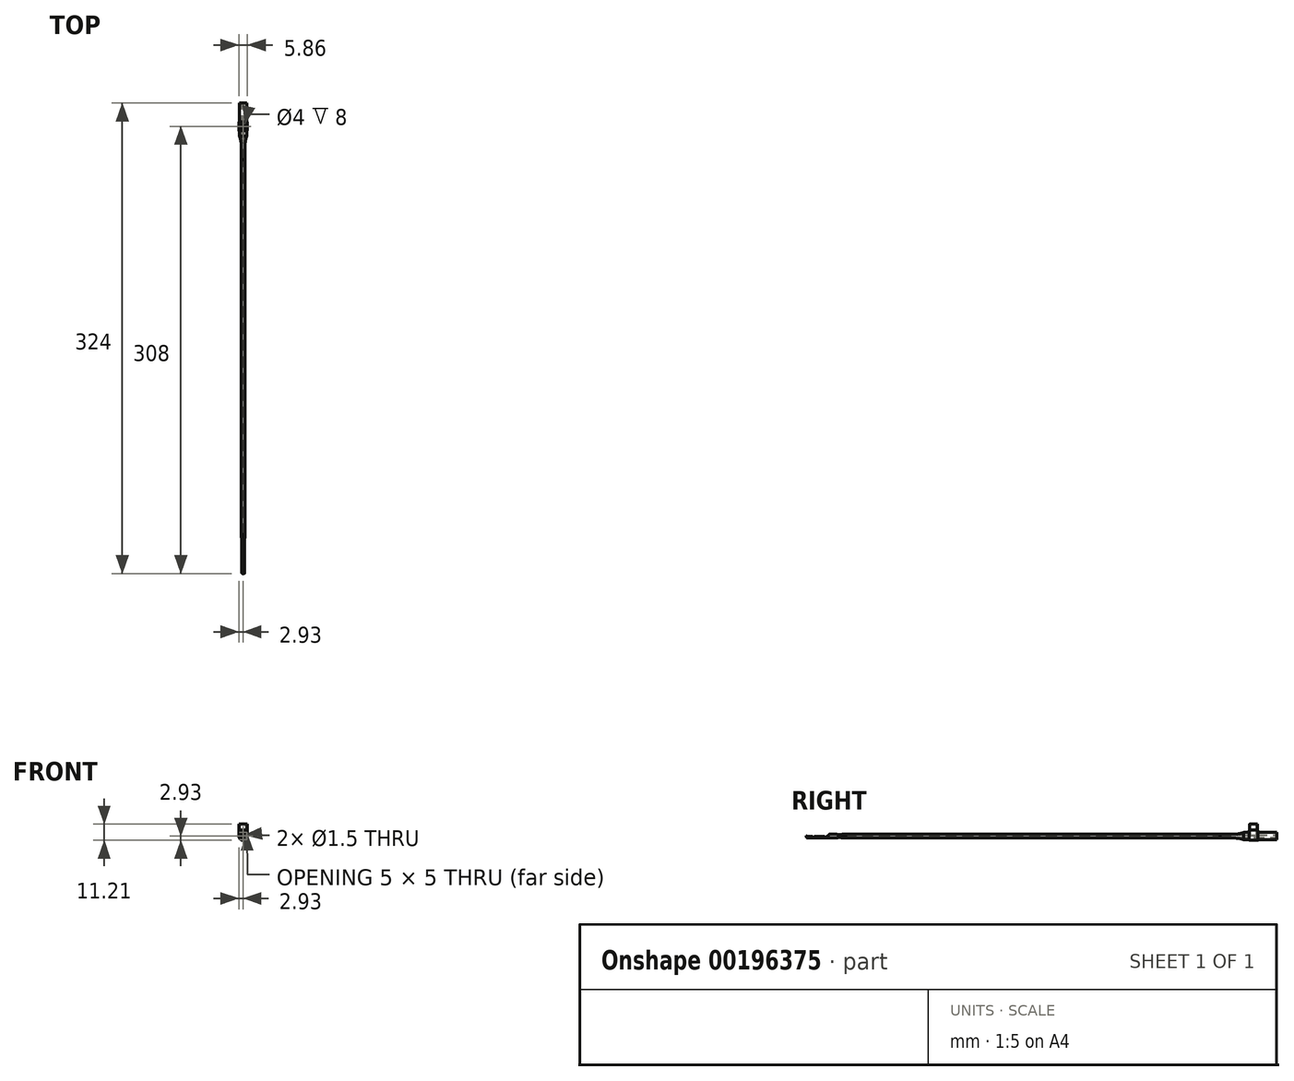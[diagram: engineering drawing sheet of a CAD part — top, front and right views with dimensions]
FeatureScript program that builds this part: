
annotation { "Feature Type Name" : "Feature", "Feature Type Description" : "" }
export const myFeature = defineFeature(function(context is Context, id is Id, definition is map)
    precondition{}
    {
        {
            var Q0;
            Q0=qCreatedBy(makeId("Front.planeOp"),FACE);
            var sketch = newSketch(context, id + "F0", { "sketchPlane" : qUnion([Q0])});
            skCircle(sketch, "E0", {"center": v(0, 0) * mm, "radius": 1.35 * mm});
            skSolve(sketch);
        }
        {
            var Q0;
            Q0=makeQuery(id+"F0.imprint","IMPRINT",FACE,{"disambiguationData":[TD([[makeQuery(id+"F0.imprint","IMPRINT",EDGE,{"derivedFrom":sQuery(id+"F0.wireOp",EDGE,"E0")}),1.0]])]});
            extrude(context, id + "F1", {"entities" : qUnion([Q0]), "depth" : 258 * mm});
        }
        {
            var Q0;
            Q0=qCreatedBy(makeId("Top.planeOp"),FACE);
            var sketch = newSketch(context, id + "F2", { "sketchPlane" : qUnion([Q0])});
            skLineSegment(sketch, "E1.0", {"start": v(1.35, 0) * mm, "end": v(0, 0) * mm});
            skLineSegment(sketch, "E2", {"start": v(1.35, 0) * mm, "end": v(1.35, 10.1) * mm});
            skLineSegment(sketch, "E3", {"start": v(2.5, 20) * mm, "end": v(0, 20) * mm});
            skLineSegment(sketch, "E4", {"start": v(2.52, 16.1) * mm, "end": v(2.5, 20) * mm});
            skArc(sketch, "E5", {"start": v(2.52, 16.1) * mm, "mid": v(1.65, 13.16) * mm, "end": v(1.35, 10.1) * mm});
            skLineSegment(sketch, "E6", {"start": v(0, 0) * mm, "end": v(0, 20) * mm, "construction": true});
            skPoint(sketch, "E7.start.orphan", {"position": v(-1.35, 0) * mm});
            skPoint(sketch, "E8.start.orphan", {"position": v(-1.35, 10.1) * mm});
            skPoint(sketch, "E9.start.orphan", {"position": v(-2.5, 16.1) * mm});
            skPoint(sketch, "E10.orphan", {"position": v(-2.5, 20) * mm});
            skLineSegment(sketch, "E11", {"start": v(0, 0) * mm, "end": v(0, 20) * mm});
            skSolve(sketch);
        }
        {
            var Q0;
            Q0 = qSketchRegion(id + "F2", true);
            var Q1;
            Q1=sQuery(id+"F2.wireOp",EDGE,"E6");
            revolve(context, id + "F3", {"entities" : qUnion([Q0]), "axis" : qUnion([Q1]), "revolveType" : RevolveType.FULL});
        }
        {
            var Q0;
            Q0=makeQuery(id+"F3.opRevolve","SWEPT_FACE",FACE,{"disambiguationData":[OSD([sQuery(id+"F2.wireOp",EDGE,"E3")])]});
            var sketch = newSketch(context, id + "F4", { "sketchPlane" : qUnion([Q0])});
            skArc(sketch, "E12", {"start": v(-2.93, 0) * mm, "mid": v(0, -2.93) * mm, "end": v(2.93, 0) * mm});
            skLineSegment(sketch, "E13", {"start": v(-2.93, 0) * mm, "end": v(-2.93, 4.07) * mm});
            skLineSegment(sketch, "E14", {"start": v(-2.93, 4.07) * mm, "end": v(2.92, 4.07) * mm});
            skLineSegment(sketch, "E15", {"start": v(2.92, 4.07) * mm, "end": v(2.93, 0) * mm});
            skCircle(sketch, "E16.0", {"center": v(0, 0) * mm, "radius": 2.5 * mm});
            skSolve(sketch);
        }
        {
            var Q0;
            Q0 = qSketchRegion(id + "F4", true);
            extrude(context, id + "F5", {"entities" : qUnion([Q0]), "operationType" : NewBodyOperationType.ADD, "depth" : 6 * mm});
        }
        {
            var Q0;
            Q0=makeQuery(id+"F5.opExtrude","SWEPT_FACE",FACE,{"disambiguationData":[OSD([sQuery(id+"F4.wireOp",EDGE,"E14")])]});
            var sketch = newSketch(context, id + "F6", { "sketchPlane" : qUnion([Q0])});
            skCircle(sketch, "E17", {"center": v(0, 23) * mm, "radius": 2.75 * mm});
            skSolve(sketch);
        }
        {
            var Q0;
            Q0 = qSketchRegion(id + "F6", true);
            extrude(context, id + "F7", {"entities" : qUnion([Q0]), "operationType" : NewBodyOperationType.ADD, "depth" : 4.2 * mm});
        }
        {
            var Q0;
            Q0=makeQuery(id+"F5.opExtrude","SWEPT_EDGE",EDGE,{"disambiguationData":[OSD([sQuery(id+"F4.wireOp",EDGE,"E13"),sQuery(id+"F4.wireOp",EDGE,"E14")])]});
            var Q1;
            Q1=makeQuery(id+"F5.opExtrude","SWEPT_EDGE",EDGE,{"disambiguationData":[OSD([sQuery(id+"F4.wireOp",EDGE,"E14"),sQuery(id+"F4.wireOp",EDGE,"E15")])]});
            var Q2;
            Q2=makeQuery(id+"F5.opExtrude","CAP_EDGE",EDGE,{"disambiguationData":[OSD([sQuery(id+"F4.wireOp",EDGE,"E14")])],"isStart":true});
            var Q3;
            Q3=makeQuery(id+"F5.opExtrude","CAP_EDGE",EDGE,{"disambiguationData":[OSD([sQuery(id+"F4.wireOp",EDGE,"E14")])],"isStart":false});
            fillet(context, id + "F8", {"entities" : qUnion([Q0, Q1, Q2, Q3]), "radius" : 1 * mm, "tangentPropagation" : true, "allowEdgeOverflow" : false});
        }
        {
            var Q0;
            Q0=makeQuery(id+"F3.opRevolve","SWEPT_FACE",FACE,{"disambiguationData":[OSD([sQuery(id+"F2.wireOp",EDGE,"E3")])]});
            extrude(context, id + "F9", {"entities" : qUnion([Q0]), "operationType" : NewBodyOperationType.ADD, "depth" : 19 * mm});
        }
        {
            var Q0;
            Q0=makeQuery(id+"F7.opExtrude","CAP_FACE",FACE,{"disambiguationData":[OSD([sQuery(id+"F6.wireOp",EDGE,"E17")])],"isStart":false});
            var sketch = newSketch(context, id + "F10", { "sketchPlane" : qUnion([Q0])});
            skCircle(sketch, "E18", {"center": v(0, 23) * mm, "radius": 2 * mm});
            skSolve(sketch);
        }
        {
            var Q0;
            Q0 = qSketchRegion(id + "F10", true);
            extrude(context, id + "F11", {"entities" : qUnion([Q0]), "operationType" : NewBodyOperationType.REMOVE, "oppositeDirection" : true, "depth" : 8 * mm});
        }
        {
            var Q0;
            Q0=makeQuery(id+"F9.opExtrude","CAP_FACE",FACE,{"disambiguationData":[OSD([sQuery(id+"F2.wireOp",EDGE,"E3")])],"isStart":false});
            var sketch = newSketch(context, id + "F12", { "sketchPlane" : qUnion([Q0])});
            skCircle(sketch, "E19", {"center": v(0, 0) * mm, "radius": 0.75 * mm});
            skSolve(sketch);
        }
        {
            var Q0;
            Q0 = qSketchRegion(id + "F12", true);
            extrude(context, id + "F13", {"entities" : qUnion([Q0]), "operationType" : NewBodyOperationType.REMOVE, "endBound" : BoundingType.THROUGH_ALL, "oppositeDirection" : true, "depth" : 25.4 * mm});
        }
        {
            var Q0;
            Q0=makeQuery(id+"F1.opExtrude","CAP_FACE",FACE,{"disambiguationData":[OSD([sQuery(id+"F0.wireOp",EDGE,"E0")])],"isStart":false});
            var sketch = newSketch(context, id + "F14", { "sketchPlane" : qUnion([Q0])});
            skCircle(sketch, "E20", {"center": v(0, 0) * mm, "radius": 1.35 * mm});
            skSolve(sketch);
        }
        {
            var Q0;
            Q0 = qSketchRegion(id + "F14", true);
            extrude(context, id + "F15", {"entities" : qUnion([Q0]), "depth" : 27 * mm});
        }
        {
            var Q0;
            Q0=qCreatedBy(makeId("Top.planeOp"),FACE);
            var sketch = newSketch(context, id + "F16", { "sketchPlane" : qUnion([Q0])});
            skLineSegment(sketch, "E21.0", {"start": v(1.35, -258) * mm, "end": v(-1.35, -258) * mm, "construction": true});
            skLineSegment(sketch, "E22", {"start": v(-1, -285) * mm, "end": v(-1, -262) * mm});
            skLineSegment(sketch, "E23", {"start": v(1, -285) * mm, "end": v(1, -262) * mm});
            skArc(sketch, "E24", {"start": v(-1, -262) * mm, "mid": v(-1.09, -260.74) * mm, "end": v(-1.35, -259.5) * mm});
            skArc(sketch, "E25", {"start": v(1.35, -259.5) * mm, "mid": v(1.09, -260.74) * mm, "end": v(1, -262) * mm});
            skLineSegment(sketch, "E26", {"start": v(1.35, -259.5) * mm, "end": v(1.35, -285) * mm});
            skLineSegment(sketch, "E27", {"start": v(1.35, -285) * mm, "end": v(1, -285) * mm});
            skLineSegment(sketch, "E28", {"start": v(-1.35, -259.5) * mm, "end": v(-1.35, -285) * mm});
            skLineSegment(sketch, "E29", {"start": v(-1.35, -285) * mm, "end": v(-1, -285) * mm});
            skPoint(sketch, "E30.start.orphan", {"position": v(0, -285) * mm});
            skSolve(sketch);
        }
        {
            var Q0;
            Q0=makeQuery(id+"F15.opExtrude","CAP_EDGE",EDGE,{"disambiguationData":[OSD([sQuery(id+"F14.wireOp",EDGE,"E20")])],"isStart":false});
            fillet(context, id + "F17", {"entities" : qUnion([Q0]), "radius" : 1 * mm, "tangentPropagation" : true, "allowEdgeOverflow" : false});
        }
        {
            var Q0;
            Q0 = qSketchRegion(id + "F16", true);
            extrude(context, id + "F18", {"entities" : qUnion([Q0]), "operationType" : NewBodyOperationType.REMOVE, "endBound" : BoundingType.THROUGH_ALL, "oppositeDirection" : true, "depth" : 25.4 * mm, "hasSecondDirection" : true, "secondDirectionBound" : SecondDirectionBoundingType.THROUGH_ALL, "secondDirectionOppositeDirection" : false, "secondDirectionDepth" : 25.4 * mm});
        }
        {
            var Q0;
            Q0=qCreatedBy(makeId("Right.planeOp"),FACE);
            var sketch = newSketch(context, id + "F19", { "sketchPlane" : qUnion([Q0])});
            skLineSegment(sketch, "E31.0", {"start": v(-258, -1.35) * mm, "end": v(-258, 1.35) * mm, "construction": true});
            skLineSegment(sketch, "E32", {"start": v(-258, 1.35) * mm, "end": v(-259.5, 1.35) * mm, "construction": true});
            skLineSegment(sketch, "E33", {"start": v(-269, 1.35) * mm, "end": v(-285.03, 1.35) * mm, "construction": true});
            skLineSegment(sketch, "E34", {"start": v(-285.03, 1.35) * mm, "end": v(-285.03, 0) * mm});
            skLineSegment(sketch, "E35", {"start": v(-285.03, 0) * mm, "end": v(-285.03, -1.35) * mm, "construction": true});
            skLineSegment(sketch, "E36", {"start": v(-285.03, -1.35) * mm, "end": v(-264.5, -1.35) * mm, "construction": true});
            skArc(sketch, "E37", {"start": v(-264.5, 1.35) * mm, "mid": v(-262, 1) * mm, "end": v(-259.5, 1.35) * mm});
            skArc(sketch, "E38", {"start": v(-259.5, -1.35) * mm, "mid": v(-262, -1) * mm, "end": v(-264.5, -1.35) * mm});
            skLineSegment(sketch, "E39", {"start": v(-259.5, -1.35) * mm, "end": v(-258, -1.35) * mm, "construction": true});
            skLineSegment(sketch, "E40", {"start": v(-264.5, 1.35) * mm, "end": v(-259.5, 1.35) * mm});
            skLineSegment(sketch, "E41", {"start": v(-264.5, -1.35) * mm, "end": v(-259.5, -1.35) * mm});
            skLineSegment(sketch, "E42", {"start": v(-269, 1.35) * mm, "end": v(-270.5, 0) * mm});
            skLineSegment(sketch, "E43", {"start": v(-270.5, 0) * mm, "end": v(-285.03, 0) * mm});
            skLineSegment(sketch, "E44", {"start": v(-285.03, 1.35) * mm, "end": v(-285.03, 1.87) * mm});
            skLineSegment(sketch, "E45", {"start": v(-285.03, 1.87) * mm, "end": v(-269, 1.87) * mm});
            skLineSegment(sketch, "E46", {"start": v(-269, 1.87) * mm, "end": v(-269, 1.35) * mm});
            skSolve(sketch);
        }
        {
            var Q0;
            Q0 = qSketchRegion(id + "F19", true);
            extrude(context, id + "F20", {"entities" : qUnion([Q0]), "operationType" : NewBodyOperationType.REMOVE, "endBound" : BoundingType.THROUGH_ALL, "oppositeDirection" : true, "depth" : 25.4 * mm, "hasSecondDirection" : true, "secondDirectionBound" : SecondDirectionBoundingType.THROUGH_ALL, "secondDirectionOppositeDirection" : false, "secondDirectionDepth" : 25.4 * mm});
        }
        {
            var Q0;
            Q0=makeQuery(id+"F18.boolean.opBoolean","INTERSECT",EDGE,{"derivedFrom":[makeQuery(id+"F15.opExtrude","SWEPT_FACE",FACE,{"disambiguationData":[OSD([sQuery(id+"F14.wireOp",EDGE,"E20")])]}),makeQuery(id+"F18.opExtrude","SWEPT_FACE",FACE,{"disambiguationData":[OSD([sQuery(id+"F16.wireOp",EDGE,"E24")])]})]});
            var Q1;
            Q1=makeQuery(id+"F20.boolean.opBoolean","INTERSECT",EDGE,{"derivedFrom":[makeQuery(id+"F15.opExtrude","SWEPT_FACE",FACE,{"disambiguationData":[OSD([sQuery(id+"F14.wireOp",EDGE,"E20")])]}),makeQuery(id+"F20.opExtrude","SWEPT_FACE",FACE,{"disambiguationData":[OSD([sQuery(id+"F19.wireOp",EDGE,"E37")])]})]});
            var Q2;
            Q2=makeQuery(id+"F18.boolean.opBoolean","INTERSECT",EDGE,{"derivedFrom":[makeQuery(id+"F15.opExtrude","SWEPT_FACE",FACE,{"disambiguationData":[OSD([sQuery(id+"F14.wireOp",EDGE,"E20")])]}),makeQuery(id+"F18.opExtrude","SWEPT_FACE",FACE,{"disambiguationData":[OSD([sQuery(id+"F16.wireOp",EDGE,"E25")])]})]});
            var Q3;
            Q3=makeQuery(id+"F18.boolean.opBoolean","COPY",EDGE,{"derivedFrom":makeQuery(id+"F18.opExtrude","SWEPT_EDGE",EDGE,{"disambiguationData":[OSD([sQuery(id+"F16.wireOp",EDGE,"E23"),sQuery(id+"F16.wireOp",EDGE,"E25")])]})});
            var Q4;
            Q4=makeQuery(id+"F18.boolean.opBoolean","COPY",EDGE,{"derivedFrom":makeQuery(id+"F18.opExtrude","SWEPT_EDGE",EDGE,{"disambiguationData":[OSD([sQuery(id+"F16.wireOp",EDGE,"E22"),sQuery(id+"F16.wireOp",EDGE,"E24")])]})});
            var Q5;
            Q5=makeQuery(id+"F20.boolean.opBoolean","INTERSECT",EDGE,{"derivedFrom":[makeQuery(id+"F15.opExtrude","SWEPT_FACE",FACE,{"disambiguationData":[OSD([sQuery(id+"F14.wireOp",EDGE,"E20")])]}),makeQuery(id+"F20.opExtrude","SWEPT_FACE",FACE,{"disambiguationData":[OSD([sQuery(id+"F19.wireOp",EDGE,"E38")])]})]});
            fillet(context, id + "F21", {"entities" : qUnion([Q0, Q1, Q2, Q3, Q4, Q5]), "radius" : .25 * mm, "tangentPropagation" : true, "allowEdgeOverflow" : false});
        }
        {
            var Q0;
            Q0=qCreatedBy(makeId("Right.planeOp"),FACE);
            var sketch = newSketch(context, id + "F22", { "sketchPlane" : qUnion([Q0])});
            skLineSegment(sketch, "E47.0", {"start": v(-269.6, 0.8) * mm, "end": v(-270.5, 0) * mm});
            skLineSegment(sketch, "E47.1", {"start": v(-270.5, 0) * mm, "end": v(-284.63, 0) * mm});
            skLineSegment(sketch, "E48", {"start": v(-270.5, 0) * mm, "end": v(-270.67, -0.15) * mm});
            skLineSegment(sketch, "E49", {"start": v(-270.67, -0.15) * mm, "end": v(-270.83, 0) * mm});
            skLineSegment(sketch, "E50.1.0.0", {"start": v(-270.83, 0) * mm, "end": v(-271, -0.15) * mm});
            skLineSegment(sketch, "E50.1.0.1", {"start": v(-271, -0.15) * mm, "end": v(-271.16, 0) * mm});
            skLineSegment(sketch, "E50.2.0.0", {"start": v(-271.16, 0) * mm, "end": v(-271.33, -0.15) * mm});
            skLineSegment(sketch, "E50.2.0.1", {"start": v(-271.33, -0.15) * mm, "end": v(-271.5, 0) * mm});
            skLineSegment(sketch, "E50.3.0.0", {"start": v(-271.5, 0) * mm, "end": v(-271.66, -0.15) * mm});
            skLineSegment(sketch, "E50.3.0.1", {"start": v(-271.66, -0.15) * mm, "end": v(-271.82, 0) * mm});
            skLineSegment(sketch, "E50.4.0.0", {"start": v(-271.82, 0) * mm, "end": v(-271.99, -0.15) * mm});
            skLineSegment(sketch, "E50.4.0.1", {"start": v(-271.99, -0.15) * mm, "end": v(-272.15, 0) * mm});
            skLineSegment(sketch, "E50.5.0.0", {"start": v(-272.15, 0) * mm, "end": v(-272.32, -0.15) * mm});
            skLineSegment(sketch, "E50.5.0.1", {"start": v(-272.32, -0.15) * mm, "end": v(-272.48, 0) * mm});
            skLineSegment(sketch, "E50.6.0.0", {"start": v(-272.48, 0) * mm, "end": v(-272.65, -0.15) * mm});
            skLineSegment(sketch, "E50.6.0.1", {"start": v(-272.65, -0.15) * mm, "end": v(-272.81, 0) * mm});
            skLineSegment(sketch, "E50.7.0.0", {"start": v(-272.81, 0) * mm, "end": v(-272.98, -0.15) * mm});
            skLineSegment(sketch, "E50.7.0.1", {"start": v(-272.98, -0.15) * mm, "end": v(-273.14, 0) * mm});
            skLineSegment(sketch, "E50.8.0.0", {"start": v(-273.14, 0) * mm, "end": v(-273.3, -0.15) * mm});
            skLineSegment(sketch, "E50.8.0.1", {"start": v(-273.3, -0.15) * mm, "end": v(-273.47, 0) * mm});
            skLineSegment(sketch, "E50.9.0.0", {"start": v(-273.47, 0) * mm, "end": v(-273.64, -0.15) * mm});
            skLineSegment(sketch, "E50.9.0.1", {"start": v(-273.64, -0.15) * mm, "end": v(-273.8, 0) * mm});
            skLineSegment(sketch, "E50.10.0.0", {"start": v(-273.8, 0) * mm, "end": v(-273.97, -0.15) * mm});
            skLineSegment(sketch, "E50.10.0.1", {"start": v(-273.97, -0.15) * mm, "end": v(-274.14, 0) * mm});
            skLineSegment(sketch, "E50.11.0.0", {"start": v(-274.13, 0) * mm, "end": v(-274.3, -0.15) * mm});
            skLineSegment(sketch, "E50.11.0.1", {"start": v(-274.3, -0.15) * mm, "end": v(-274.47, 0) * mm});
            skLineSegment(sketch, "E50.12.0.0", {"start": v(-274.46, 0) * mm, "end": v(-274.63, -0.15) * mm});
            skLineSegment(sketch, "E50.12.0.1", {"start": v(-274.63, -0.15) * mm, "end": v(-274.8, 0) * mm});
            skLineSegment(sketch, "E50.13.0.0", {"start": v(-274.8, 0) * mm, "end": v(-274.96, -0.15) * mm});
            skLineSegment(sketch, "E50.13.0.1", {"start": v(-274.96, -0.15) * mm, "end": v(-275.13, 0) * mm});
            skLineSegment(sketch, "E50.14.0.0", {"start": v(-275.12, 0) * mm, "end": v(-275.29, -0.15) * mm});
            skLineSegment(sketch, "E50.14.0.1", {"start": v(-275.29, -0.15) * mm, "end": v(-275.46, 0) * mm});
            skLineSegment(sketch, "E50.15.0.0", {"start": v(-275.45, 0) * mm, "end": v(-275.62, -0.15) * mm});
            skLineSegment(sketch, "E50.15.0.1", {"start": v(-275.62, -0.15) * mm, "end": v(-275.79, 0) * mm});
            skLineSegment(sketch, "E50.16.0.0", {"start": v(-275.78, 0) * mm, "end": v(-275.95, -0.15) * mm});
            skLineSegment(sketch, "E50.16.0.1", {"start": v(-275.95, -0.15) * mm, "end": v(-276.12, 0) * mm});
            skLineSegment(sketch, "E50.17.0.0", {"start": v(-276.11, 0) * mm, "end": v(-276.28, -0.15) * mm});
            skLineSegment(sketch, "E50.17.0.1", {"start": v(-276.28, -0.15) * mm, "end": v(-276.45, 0) * mm});
            skLineSegment(sketch, "E50.18.0.0", {"start": v(-276.44, 0) * mm, "end": v(-276.61, -0.15) * mm});
            skLineSegment(sketch, "E50.18.0.1", {"start": v(-276.61, -0.15) * mm, "end": v(-276.78, 0) * mm});
            skLineSegment(sketch, "E50.19.0.0", {"start": v(-276.77, 0) * mm, "end": v(-276.94, -0.15) * mm});
            skLineSegment(sketch, "E50.19.0.1", {"start": v(-276.94, -0.15) * mm, "end": v(-277.1, 0) * mm});
            skLineSegment(sketch, "E50.20.0.0", {"start": v(-277.1, 0) * mm, "end": v(-277.27, -0.15) * mm});
            skLineSegment(sketch, "E50.20.0.1", {"start": v(-277.27, -0.15) * mm, "end": v(-277.44, 0) * mm});
            skLineSegment(sketch, "E50.21.0.0", {"start": v(-277.43, 0) * mm, "end": v(-277.6, -0.15) * mm});
            skLineSegment(sketch, "E50.21.0.1", {"start": v(-277.6, -0.15) * mm, "end": v(-277.77, 0) * mm});
            skLineSegment(sketch, "E50.22.0.0", {"start": v(-277.76, 0) * mm, "end": v(-277.93, -0.15) * mm});
            skLineSegment(sketch, "E50.22.0.1", {"start": v(-277.93, -0.15) * mm, "end": v(-278.1, 0) * mm});
            skLineSegment(sketch, "E50.23.0.0", {"start": v(-278.1, 0) * mm, "end": v(-278.26, -0.15) * mm});
            skLineSegment(sketch, "E50.23.0.1", {"start": v(-278.26, -0.15) * mm, "end": v(-278.43, 0) * mm});
            skLineSegment(sketch, "E50.24.0.0", {"start": v(-278.42, 0) * mm, "end": v(-278.6, -0.15) * mm});
            skLineSegment(sketch, "E50.24.0.1", {"start": v(-278.6, -0.15) * mm, "end": v(-278.76, 0) * mm});
            skLineSegment(sketch, "E50.25.0.0", {"start": v(-278.75, 0) * mm, "end": v(-278.92, -0.15) * mm});
            skLineSegment(sketch, "E50.25.0.1", {"start": v(-278.92, -0.15) * mm, "end": v(-279.09, 0) * mm});
            skLineSegment(sketch, "E50.26.0.0", {"start": v(-279.09, 0) * mm, "end": v(-279.25, -0.15) * mm});
            skLineSegment(sketch, "E50.26.0.1", {"start": v(-279.25, -0.15) * mm, "end": v(-279.42, 0) * mm});
            skLineSegment(sketch, "E50.27.0.0", {"start": v(-279.42, 0) * mm, "end": v(-279.58, -0.15) * mm});
            skLineSegment(sketch, "E50.27.0.1", {"start": v(-279.58, -0.15) * mm, "end": v(-279.75, 0) * mm});
            skLineSegment(sketch, "E50.28.0.0", {"start": v(-279.75, 0) * mm, "end": v(-279.91, -0.15) * mm});
            skLineSegment(sketch, "E50.28.0.1", {"start": v(-279.91, -0.15) * mm, "end": v(-280.08, 0) * mm});
            skLineSegment(sketch, "E50.29.0.0", {"start": v(-280.08, 0) * mm, "end": v(-280.24, -0.15) * mm});
            skLineSegment(sketch, "E50.29.0.1", {"start": v(-280.24, -0.15) * mm, "end": v(-280.4, 0) * mm});
            skLineSegment(sketch, "E50.30.0.0", {"start": v(-280.4, 0) * mm, "end": v(-280.57, -0.15) * mm});
            skLineSegment(sketch, "E50.30.0.1", {"start": v(-280.57, -0.15) * mm, "end": v(-280.74, 0) * mm});
            skLineSegment(sketch, "E50.31.0.0", {"start": v(-280.74, 0) * mm, "end": v(-280.9, -0.15) * mm});
            skLineSegment(sketch, "E50.31.0.1", {"start": v(-280.9, -0.15) * mm, "end": v(-281.07, 0) * mm});
            skLineSegment(sketch, "E50.32.0.0", {"start": v(-281.07, 0) * mm, "end": v(-281.23, -0.15) * mm});
            skLineSegment(sketch, "E50.32.0.1", {"start": v(-281.23, -0.15) * mm, "end": v(-281.4, 0) * mm});
            skLineSegment(sketch, "E50.33.0.0", {"start": v(-281.4, 0) * mm, "end": v(-281.56, -0.15) * mm});
            skLineSegment(sketch, "E50.33.0.1", {"start": v(-281.56, -0.15) * mm, "end": v(-281.73, 0) * mm});
            skLineSegment(sketch, "E50.34.0.0", {"start": v(-281.73, 0) * mm, "end": v(-281.9, -0.15) * mm});
            skLineSegment(sketch, "E50.34.0.1", {"start": v(-281.9, -0.15) * mm, "end": v(-282.06, 0) * mm});
            skLineSegment(sketch, "E50.35.0.0", {"start": v(-282.06, 0) * mm, "end": v(-282.22, -0.15) * mm});
            skLineSegment(sketch, "E50.35.0.1", {"start": v(-282.22, -0.15) * mm, "end": v(-282.4, 0) * mm});
            skLineSegment(sketch, "E50.36.0.0", {"start": v(-282.39, 0) * mm, "end": v(-282.55, -0.15) * mm});
            skLineSegment(sketch, "E50.36.0.1", {"start": v(-282.55, -0.15) * mm, "end": v(-282.72, 0) * mm});
            skLineSegment(sketch, "E50.37.0.0", {"start": v(-282.72, 0) * mm, "end": v(-282.88, -0.15) * mm});
            skLineSegment(sketch, "E50.37.0.1", {"start": v(-282.88, -0.15) * mm, "end": v(-283.05, 0) * mm});
            skLineSegment(sketch, "E50.38.0.0", {"start": v(-283.05, 0) * mm, "end": v(-283.21, -0.15) * mm});
            skLineSegment(sketch, "E50.38.0.1", {"start": v(-283.21, -0.15) * mm, "end": v(-283.38, 0) * mm});
            skLineSegment(sketch, "E50.39.0.0", {"start": v(-283.38, 0) * mm, "end": v(-283.54, -0.15) * mm});
            skLineSegment(sketch, "E50.39.0.1", {"start": v(-283.54, -0.15) * mm, "end": v(-283.71, 0) * mm});
            skLineSegment(sketch, "E50.40.0.0", {"start": v(-283.7, 0) * mm, "end": v(-283.87, -0.15) * mm});
            skLineSegment(sketch, "E50.40.0.1", {"start": v(-283.87, -0.15) * mm, "end": v(-284.04, 0) * mm});
            skLineSegment(sketch, "E50.41.0.0", {"start": v(-284.04, 0) * mm, "end": v(-284.2, -0.15) * mm});
            skLineSegment(sketch, "E50.41.0.1", {"start": v(-284.2, -0.15) * mm, "end": v(-284.37, 0) * mm});
            skLineSegment(sketch, "E50.42.0.0", {"start": v(-284.37, 0) * mm, "end": v(-284.54, -0.15) * mm});
            skLineSegment(sketch, "E50.42.0.1", {"start": v(-284.54, -0.15) * mm, "end": v(-284.7, 0) * mm});
            skLineSegment(sketch, "E50.43.0.0", {"start": v(-284.7, 0) * mm, "end": v(-284.87, -0.15) * mm});
            skLineSegment(sketch, "E50.43.0.1", {"start": v(-284.87, -0.15) * mm, "end": v(-285.03, 0) * mm});
            skLineSegment(sketch, "E50.44.0.0", {"start": v(-285.03, 0) * mm, "end": v(-285.2, -0.15) * mm});
            skLineSegment(sketch, "E50.44.0.1", {"start": v(-285.2, -0.15) * mm, "end": v(-285.36, 0) * mm});
            skLineSegment(sketch, "E50.45.0.0", {"start": v(-285.36, 0) * mm, "end": v(-285.53, -0.15) * mm});
            skLineSegment(sketch, "E50.45.0.1", {"start": v(-285.53, -0.15) * mm, "end": v(-285.7, 0) * mm});
            skLineSegment(sketch, "E50.direction1", {"start": v(-270.83, 0) * mm, "end": v(-271.16, 0) * mm, "construction": true});
            skLineSegment(sketch, "E51.0.46.0", {"start": v(-285.69, 0) * mm, "end": v(-285.86, -0.15) * mm});
            skLineSegment(sketch, "E51.3.46.0", {"start": v(-285.86, -0.15) * mm, "end": v(-286.02, 0) * mm});
            skLineSegment(sketch, "E52", {"start": v(-270.5, 0) * mm, "end": v(-286.02, 0) * mm});
            skSolve(sketch);
        }
        {
            var Q0;
            Q0 = qSketchRegion(id + "F22", true);
            extrude(context, id + "F23", {"entities" : qUnion([Q0]), "operationType" : NewBodyOperationType.REMOVE, "endBound" : BoundingType.THROUGH_ALL, "oppositeDirection" : true, "depth" : 25.4 * mm, "hasSecondDirection" : true, "secondDirectionBound" : SecondDirectionBoundingType.THROUGH_ALL, "secondDirectionOppositeDirection" : false, "secondDirectionDepth" : 25.4 * mm});
        }
    });
